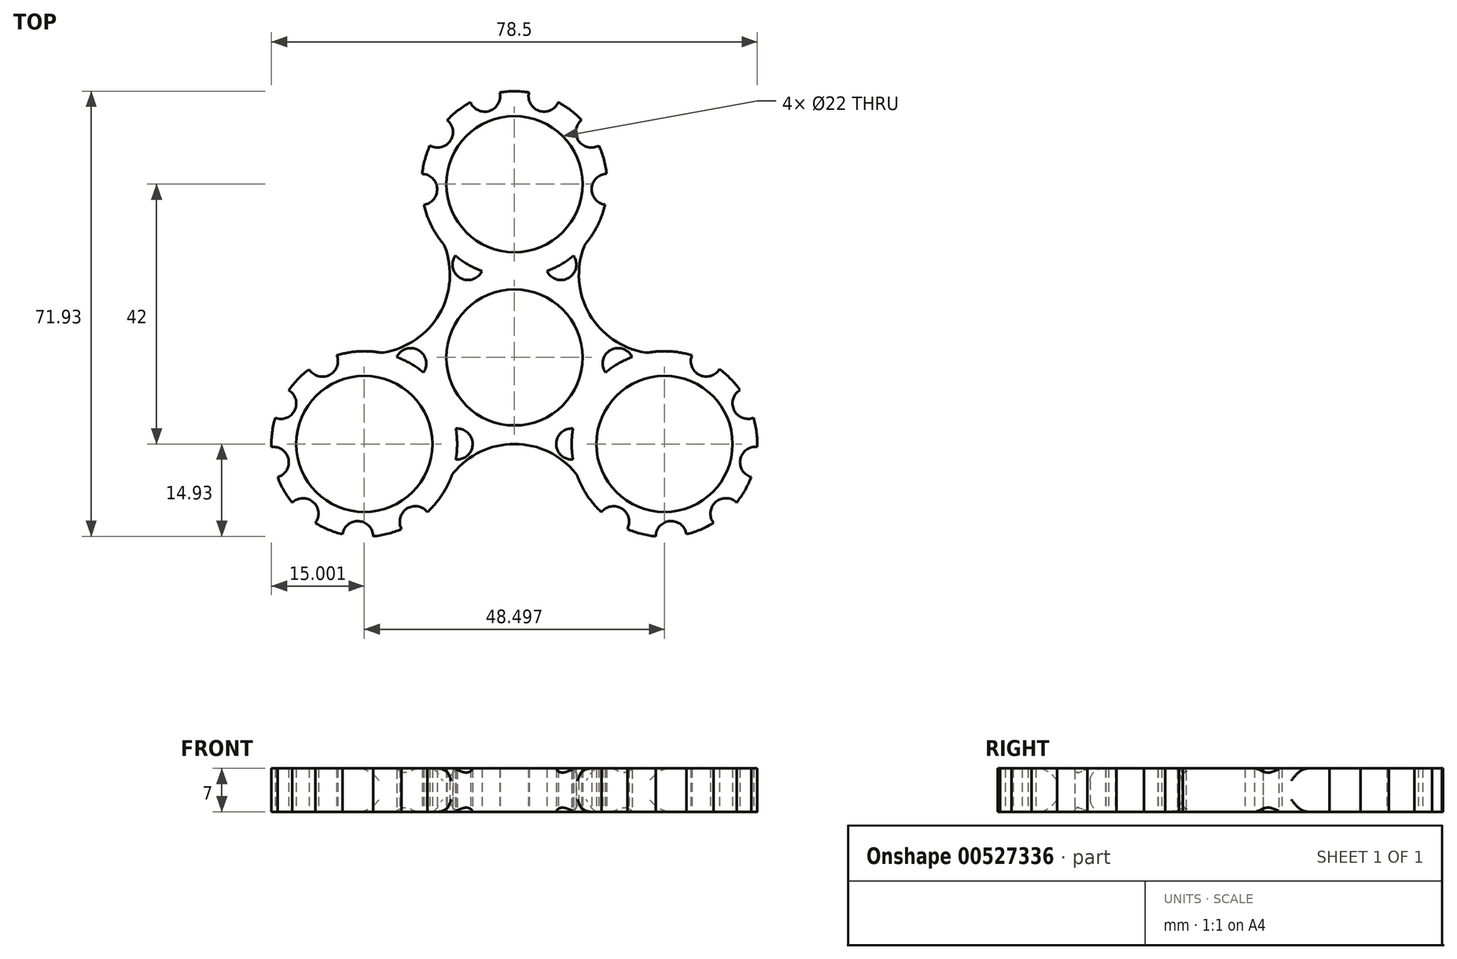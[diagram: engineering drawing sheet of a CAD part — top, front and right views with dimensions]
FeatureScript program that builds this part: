
annotation { "Feature Type Name" : "Feature", "Feature Type Description" : "" }
export const myFeature = defineFeature(function(context is Context, id is Id, definition is map)
    precondition{}
    {
        {
            var Q0;
            Q0=qCreatedBy(makeId("Top.planeOp"),FACE);
            var sketch = newSketch(context, id + "F0", { "sketchPlane" : qUnion([Q0])});
            skCircle(sketch, "E0", {"center": v(0, 0) * mm, "radius": 11 * mm});
            skCircle(sketch, "E1", {"center": v(0, 28) * mm, "radius": 11 * mm});
            skCircle(sketch, "E2.0", {"center": v(0, 28) * mm, "radius": 15 * mm});
            skCircle(sketch, "E3.1.0", {"center": v(-24.25, -14) * mm, "radius": 15 * mm});
            skCircle(sketch, "E3.1.1", {"center": v(-24.25, -14) * mm, "radius": 11 * mm});
            skCircle(sketch, "E3.2.0", {"center": v(24.25, -14) * mm, "radius": 15 * mm});
            skCircle(sketch, "E3.2.1", {"center": v(24.25, -14) * mm, "radius": 11 * mm});
            skArc(sketch, "E4", {"start": v(-9.55, 16.44) * mm, "mid": v(-8.75, 12.84) * mm, "end": v(-5.24, 13.94) * mm});
            skPoint(sketch, "E5.orphan", {"position": v(-12.35, 16.61) * mm});
            skPoint(sketch, "E6.orphan", {"position": v(-8.02, 14.11) * mm});
            skArc(sketch, "E7.MirrorCS", {"start": v(-19.01, 0.06) * mm, "mid": v(-15.5, 1.16) * mm, "end": v(-14.7, -2.44) * mm});
            skArc(sketch, "E8", {"start": v(-13.58, 4.97) * mm, "mid": v(-9.96, 5.75) * mm, "end": v(-11.1, 9.28) * mm});
            skLineSegment(sketch, "E9", {"start": v(0, 0) * mm, "end": v(-9.96, 5.75) * mm});
            skArc(sketch, "E10", {"start": v(-21.5, 0.75) * mm, "mid": v(-12.12, 7) * mm, "end": v(-11.4, 18.25) * mm});
            skArc(sketch, "E11.1.0", {"start": v(10.1, -19) * mm, "mid": v(0, -14) * mm, "end": v(-10.1, -19) * mm});
            skArc(sketch, "E11.1.1", {"start": v(-9.46, -16.5) * mm, "mid": v(-6.75, -14) * mm, "end": v(-9.46, -11.5) * mm});
            skArc(sketch, "E11.1.2", {"start": v(2.49, -14.25) * mm, "mid": v(0, -11.5) * mm, "end": v(-2.49, -14.25) * mm});
            skArc(sketch, "E11.1.3", {"start": v(9.46, -16.5) * mm, "mid": v(6.75, -14) * mm, "end": v(9.46, -11.5) * mm});
            skArc(sketch, "E11.2.0", {"start": v(11.4, 18.25) * mm, "mid": v(12.12, 7) * mm, "end": v(21.5, 0.75) * mm});
            skArc(sketch, "E11.2.1", {"start": v(19.01, 0.06) * mm, "mid": v(15.5, 1.16) * mm, "end": v(14.7, -2.44) * mm});
            skArc(sketch, "E11.2.2", {"start": v(11.1, 9.28) * mm, "mid": v(9.96, 5.75) * mm, "end": v(13.58, 4.97) * mm});
            skArc(sketch, "E11.2.3", {"start": v(9.55, 16.44) * mm, "mid": v(8.75, 12.84) * mm, "end": v(5.24, 13.94) * mm});
            skLineSegment(sketch, "E12", {"start": v(0, 28) * mm, "end": v(-11.4, 18.25) * mm});
            skLineSegment(sketch, "E13.MirrorCS", {"start": v(0, 28) * mm, "end": v(11.4, 18.25) * mm});
            skCircle(sketch, "E14.1.0", {"center": v(-14.98, 27.15) * mm, "radius": 2.5 * mm});
            skCircle(sketch, "E14.2.0", {"center": v(-12.43, 36.4) * mm, "radius": 2.5 * mm});
            skCircle(sketch, "E14.3.0", {"center": v(-4.8, 42.21) * mm, "radius": 2.5 * mm});
            skCircle(sketch, "E14.4.0", {"center": v(4.79, 42.22) * mm, "radius": 2.5 * mm});
            skCircle(sketch, "E14.5.0", {"center": v(12.42, 36.4) * mm, "radius": 2.5 * mm});
            skCircle(sketch, "E14.6.0", {"center": v(14.98, 27.17) * mm, "radius": 2.5 * mm});
            skLineSegment(sketch, "E14.anchor1", {"start": v(0, 28) * mm, "end": v(-11.4, 18.25) * mm, "construction": true});
            skLineSegment(sketch, "E14.anchor2", {"start": v(0, 28) * mm, "end": v(11.41, 18.26) * mm, "construction": true});
            skCircle(sketch, "E15.1.0", {"center": v(-16.03, -26.55) * mm, "radius": 2.5 * mm});
            skCircle(sketch, "E15.1.1", {"center": v(-25.3, -28.96) * mm, "radius": 2.5 * mm});
            skCircle(sketch, "E15.1.2", {"center": v(-34.15, -25.26) * mm, "radius": 2.5 * mm});
            skCircle(sketch, "E15.1.3", {"center": v(-38.95, -16.96) * mm, "radius": 2.5 * mm});
            skCircle(sketch, "E15.1.4", {"center": v(-37.74, -7.45) * mm, "radius": 2.5 * mm});
            skCircle(sketch, "E15.1.5", {"center": v(-31.02, -0.61) * mm, "radius": 2.5 * mm});
            skCircle(sketch, "E15.2.0", {"center": v(31, -0.6) * mm, "radius": 2.5 * mm});
            skCircle(sketch, "E15.2.1", {"center": v(37.74, -7.43) * mm, "radius": 2.5 * mm});
            skCircle(sketch, "E15.2.2", {"center": v(38.96, -16.95) * mm, "radius": 2.5 * mm});
            skCircle(sketch, "E15.2.3", {"center": v(34.17, -25.25) * mm, "radius": 2.5 * mm});
            skCircle(sketch, "E15.2.4", {"center": v(25.32, -28.96) * mm, "radius": 2.5 * mm});
            skCircle(sketch, "E15.2.5", {"center": v(16.04, -26.55) * mm, "radius": 2.5 * mm});
            skSolve(sketch);
        }
        {
            var Q0;
            Q0=makeQuery(id+"F0.imprint","IMPRINT",FACE,{"disambiguationData":[TD([[makeQuery(id+"F0.imprint","IMPRINT",EDGE,{"derivedFrom":sQuery(id+"F0.wireOp",EDGE,"E0")}),-1.0]])]});
            var Q1;
            {var subQ6=sQuery(id+"F0.wireOp",EDGE,"E1");var subQ8=sQuery(id+"F0.wireOp",EDGE,"E12");var subQ12=makeQuery(id+"F0.imprint","INTERSECT",VERTEX,{"derivedFrom":[subQ6,subQ8]});Q1=makeQuery(id+"F0.imprint","IMPRINT",FACE,{"disambiguationData":[TD([[makeQuery(id+"F0.imprint","IMPRINT",EDGE,{"disambiguationData":[TD([[subQ12,-1.0]])],"derivedFrom":subQ6}),-1.0]])]});}
            var Q2;
            {var subQ3=sQuery(id+"F0.wireOp",EDGE,"E1");var subQ14=sQuery(id+"F0.wireOp",EDGE,"E12");var subQ16=makeQuery(id+"F0.imprint","INTERSECT",VERTEX,{"derivedFrom":[subQ3,subQ14]});Q2=makeQuery(id+"F0.imprint","IMPRINT",FACE,{"disambiguationData":[TD([[makeQuery(id+"F0.imprint","IMPRINT",EDGE,{"disambiguationData":[TD([[subQ16,1.0]])],"derivedFrom":subQ3}),-1.0]])]});}
            var Q3;
            Q3=makeQuery(id+"F0.imprint","IMPRINT",FACE,{"disambiguationData":[TD([[makeQuery(id+"F0.imprint","IMPRINT",EDGE,{"derivedFrom":sQuery(id+"F0.wireOp",EDGE,"E3.1.1")}),-1.0]])]});
            var Q4;
            Q4=makeQuery(id+"F0.imprint","IMPRINT",FACE,{"disambiguationData":[TD([[makeQuery(id+"F0.imprint","IMPRINT",EDGE,{"derivedFrom":sQuery(id+"F0.wireOp",EDGE,"E3.2.1")}),-1.0]])]});
            var Q5;
            {var subQ1=sQuery(id+"F0.wireOp",EDGE,"E8");var subQ3=makeQuery(id+"F0.imprint","IMPRINT",VERTEX,{"derivedFrom":subQ1});Q5=makeQuery(id+"F0.imprint","IMPRINT",FACE,{"disambiguationData":[TD([[makeQuery(id+"F0.imprint","IMPRINT",EDGE,{"disambiguationData":[TD([[subQ3,1.0]])],"derivedFrom":subQ1}),1.0]])]});}
            var Q6;
            {var subQ0=sQuery(id+"F0.wireOp",EDGE,"E11.2.2");Q6=makeQuery(id+"F0.imprint","IMPRINT",FACE,{"disambiguationData":[TD([[makeQuery(id+"F0.imprint","IMPRINT",EDGE,{"derivedFrom":subQ0}),1.0]])]});}
            var Q7;
            {var subQ0=sQuery(id+"F0.wireOp",EDGE,"E11.1.2");Q7=makeQuery(id+"F0.imprint","IMPRINT",FACE,{"disambiguationData":[TD([[makeQuery(id+"F0.imprint","IMPRINT",EDGE,{"derivedFrom":subQ0}),1.0]])]});}
            extrude(context, id + "F1", {"entities" : qUnion([Q0, Q1, Q2, Q3, Q4, Q5, Q6, Q7]), "endBound" : BoundingType.SYMMETRIC, "depth" : 7 * mm, "offsetDistance" : 25 * mm});
        }
        {
            var Q0;
            Q0=makeQuery(id+"F1.opExtrude","SWEPT_FACE",FACE,{"disambiguationData":[OSD([sQuery(id+"F0.wireOp",EDGE,"E11.2.0")])]});
            var Q1;
            Q1=makeQuery(id+"F1.opExtrude","SWEPT_FACE",FACE,{"disambiguationData":[OSD([sQuery(id+"F0.wireOp",EDGE,"E10")])]});
            var Q2;
            Q2=makeQuery(id+"F1.opExtrude","SWEPT_FACE",FACE,{"disambiguationData":[OSD([sQuery(id+"F0.wireOp",EDGE,"E11.1.0")])]});
            fillet(context, id + "F2", {"entities" : qUnion([Q0, Q1, Q2]), "radius" : 2 * mm, "tangentPropagation" : true, "allowEdgeOverflow" : false});
        }
    });
